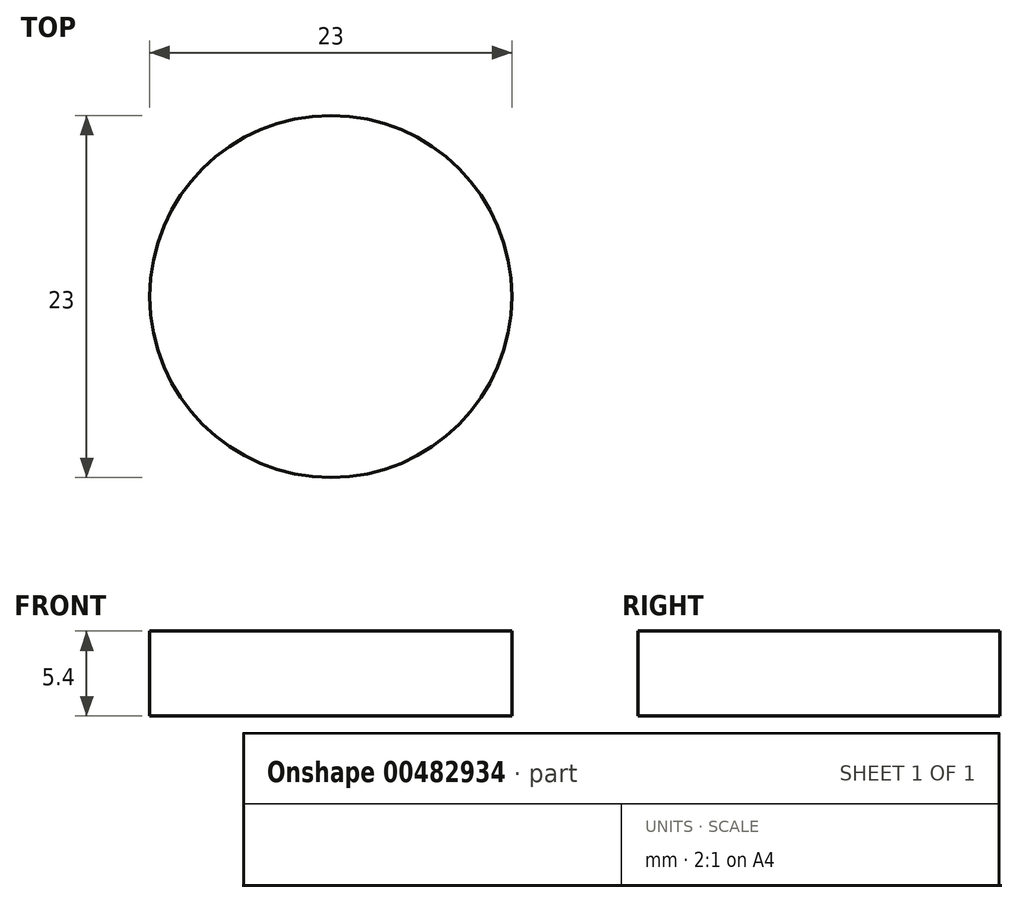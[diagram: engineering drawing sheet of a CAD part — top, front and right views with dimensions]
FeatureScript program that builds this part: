
annotation { "Feature Type Name" : "Feature", "Feature Type Description" : "" }
export const myFeature = defineFeature(function(context is Context, id is Id, definition is map)
    precondition{}
    {
        {
            var Q0;
            Q0=qCreatedBy(makeId("Top.planeOp"),FACE);
            var sketch = newSketch(context, id + "F0", { "sketchPlane" : qUnion([Q0])});
            skCircle(sketch, "E0", {"center": v(0, 0) * mm, "radius": 11.5 * mm});
            skSolve(sketch);
        }
        {
            var Q0;
            Q0 = qSketchRegion(id + "F0", true);
            extrude(context, id + "F1", {"entities" : qUnion([Q0]), "depth" : 5.4 * mm, "offsetDistance" : 25 * mm});
        }
    });
